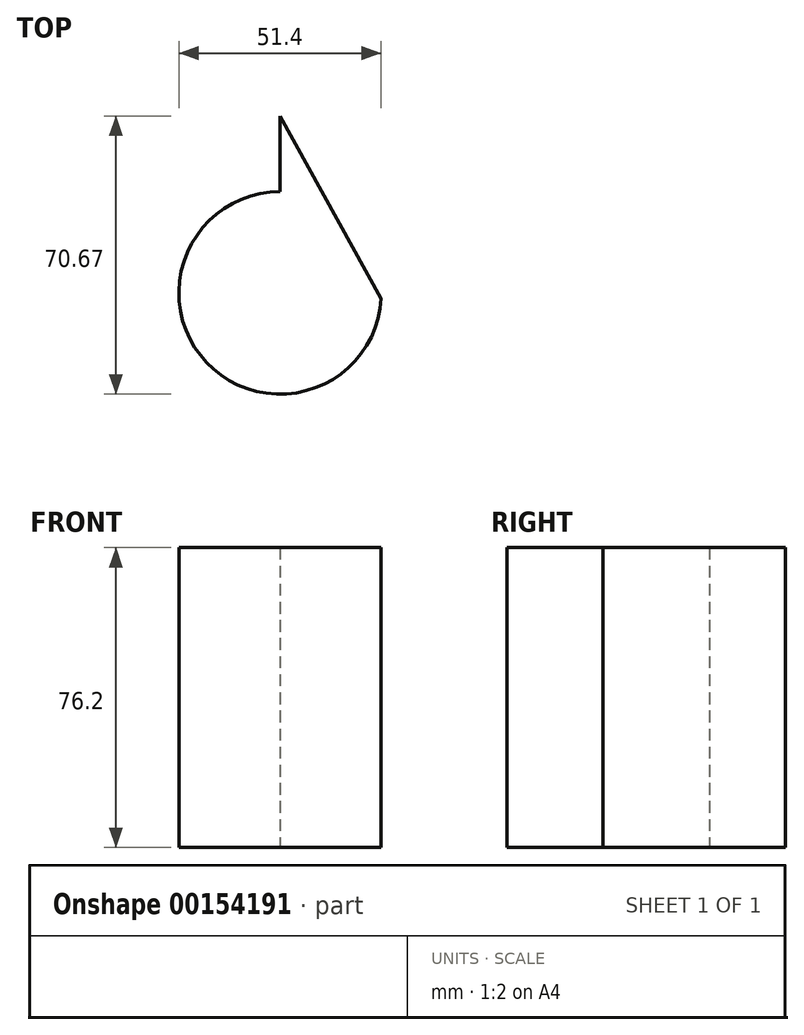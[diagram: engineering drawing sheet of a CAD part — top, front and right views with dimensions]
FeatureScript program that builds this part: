
annotation { "Feature Type Name" : "Feature", "Feature Type Description" : "" }
export const myFeature = defineFeature(function(context is Context, id is Id, definition is map)
    precondition{}
    {
        {
            var Q0;
            Q0=qCreatedBy(makeId("Top.planeOp"),FACE);
            var sketch = newSketch(context, id + "F0", { "sketchPlane" : qUnion([Q0])});
            skArc(sketch, "E0", {"start": v(0, 27.15) * mm, "mid": v(-18.68, -16.24) * mm, "end": v(25.68, 0) * mm});
            skLineSegment(sketch, "E1", {"start": v(0, 27.15) * mm, "end": v(0, 46.4) * mm});
            skLineSegment(sketch, "E2", {"start": v(0, 46.4) * mm, "end": v(25.68, 0) * mm});
            skSolve(sketch);
        }
        {
            var Q0;
            Q0=makeQuery(id+"F0.imprint","IMPRINT",FACE,{"disambiguationData":[TD([[makeQuery(id+"F0.imprint","IMPRINT",EDGE,{"derivedFrom":sQuery(id+"F0.wireOp",EDGE,"E0")}),1.0]])]});
            extrude(context, id + "F1", {"entities" : qUnion([Q0]), "depth" : 76.2 * mm});
        }
    });
